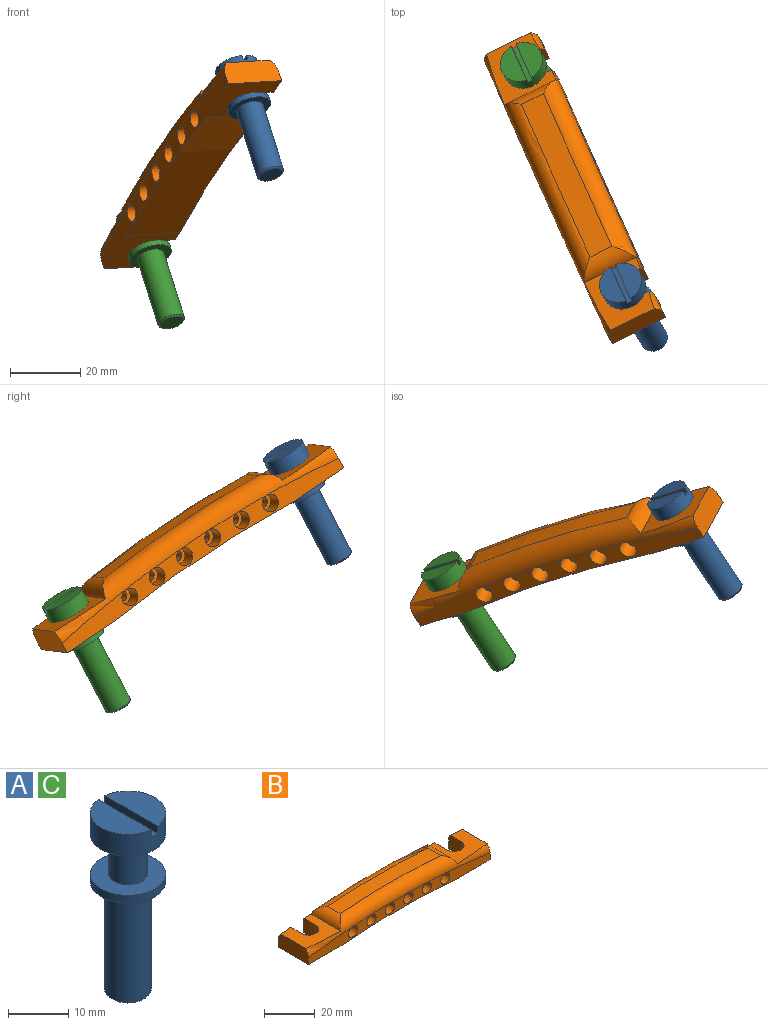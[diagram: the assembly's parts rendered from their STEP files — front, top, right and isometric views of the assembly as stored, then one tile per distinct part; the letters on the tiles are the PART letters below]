
ASSEMBLY  parts=3 mates=1
PART A: 14 faces, bbox 12.5x12.5x36.3 mm
  f0: cylinder r=6.25mm len=12.5mm, axis (0,0,-1), area 168.3mm2, adj f1,f9,f10,f11,f12,f13
  f1: plane 12.41x5.5mm, normal (0,0,1), area 52mm2, adj f0,f13
  f2: plane 6.8x6.8mm, normal (0,0,-1), area 36.3mm2, adj f3
  f3: cone r=3.9mm half-angle=45deg, axis (0,0,1), area 16.2mm2, adj f2,f4
  f4: cylinder r=3.9mm len=21.8mm, axis (0,0,-1), area 534.2mm2, adj f3,f5
  f5: plane 12.5x12.5mm, normal (0,0,-1), area 74.9mm2, adj f4,f6
  f6: cylinder r=6.25mm len=12.5mm, axis (0,0,-1), area 62.8mm2, adj f5,f7
  f7: plane 12.5x12.5mm, normal (0,0,1), area 90.5mm2, adj f6,f8
  f8: cylinder r=3.2mm len=8mm, axis (0,0,-1), area 160.8mm2, adj f7,f9
  f9: plane 12.5x12.5mm, normal (0,0,-1), area 90.5mm2, adj f0,f8
  f10: plane 12.41x5.5mm, normal (0,0,1), area 52mm2, adj f0,f12
  f11: plane 12.5x1.5mm, normal (0,0,1), area 18.7mm2, adj f0,f12,f13
  f12: plane 12.41x1.5mm, normal (-1,0,0), area 18.6mm2, adj f0,f10,f11
  f13: plane 12.41x1.5mm, normal (1,0,0), area 18.6mm2, adj f0,f1,f11
PART B: 42 faces, bbox 103.9x17.1x16 mm
  f0: cylinder r=1.5mm len=12mm, axis (0,1,0), area 113.1mm2, adj f11,f33
  f1: cylinder r=1.5mm len=12mm, axis (0,1,0), area 113.1mm2, adj f11,f41
  f2: cylinder r=1.5mm len=12mm, axis (0,1,0), area 113.1mm2, adj f11,f39
  f3: cylinder r=1.5mm len=12mm, axis (0,1,0), area 113.1mm2, adj f11,f37
  f4: cylinder r=1.5mm len=12mm, axis (0,1,0), area 113.1mm2, adj f11,f35
  f5: cylinder r=1.5mm len=12mm, axis (0,1,0), area 113.1mm2, adj f11,f31
  f6: torus R=351mm, axis (0,-1,0), area 585.5mm2, adj f7,f8,f16,f17,f18,f20,f22,f23
  f7: plane 18.24x16.62mm, normal (0,0,1), area 205.5mm2, adj f6,f13,f14,f16,f23,f27,f28,f29
  f8: plane 18.24x16.62mm, normal (0,0,1), area 205.5mm2, adj f6,f14,f15,f18,f22,f24,f25,f26
  f9: plane 18.15x17mm, normal (0,0,-1), area 227.4mm2, adj f11,f12,f18,f19,f20,f24,f25,f26
  f10: plane 18.15x17mm, normal (0,0,-1), area 227.4mm2, adj f11,f16,f19,f20,f21,f27,f28,f29
  f11: plane 73x6.99mm, normal (0,1,0), area 356.9mm2, adj f0,f1,f2,f3,f4,f5,f9,f10
  f12: plane 6.15x4.15mm, normal (0,1,0), area 23mm2, adj f9,f15,f18,f26
  f13: torus R=351mm, axis (0,-1,0), area 22.1mm2, adj f7,f16,f21,f28
  f14: torus R=351mm, axis (0,-1,0), area 502.2mm2, adj f7,f8,f11,f17,f22,f23,f25,f29
  f15: torus R=351mm, axis (0,-1,0), area 22.1mm2, adj f8,f12,f18,f26
  f16: plane 17.05x7.05mm, normal (1,0,0), area 115.4mm2, adj f6,f7,f10,f13,f20,f21
  f17: cylinder r=356mm len=56.03mm, axis (0,1,0), area 392.6mm2, adj f6,f14,f22,f23
  f18: plane 17.05x7.05mm, normal (-1,0,0), area 115.4mm2, adj f6,f8,f9,f12,f15,f20
  f19: cylinder r=356mm len=65mm, axis (0,1,0), area 1106.5mm2, adj f9,f10,f11,f20
  f20: plane 101.3x6.99mm, normal (0,-1,0), area 397mm2, adj f6,f9,f10,f16,f18,f19,f30,f32
  f21: plane 6.15x4.15mm, normal (0,1,0), area 23mm2, adj f10,f13,f16,f28
  f22: cylinder r=5mm len=16.53mm, axis (0,-1,0), area 79.5mm2, adj f6,f8,f14,f17
  f23: cylinder r=5mm len=16.53mm, axis (0,-1,0), area 79.5mm2, adj f6,f7,f14,f17
  f24: cylinder r=4mm len=8mm, axis (0,0,1), area 88mm2, adj f8,f9,f25,f26
  f25: plane 7.01x7.01mm, normal (-1,0,0), area 48.8mm2, adj f8,f9,f11,f14,f24
  f26: plane 7.02x7.02mm, normal (1,0,0), area 48.2mm2, adj f8,f9,f12,f15,f24
  f27: cylinder r=4mm len=8mm, axis (0,0,1), area 88mm2, adj f7,f10,f28,f29
  f28: plane 7.02x7.02mm, normal (-1,0,0), area 48.2mm2, adj f7,f10,f13,f21,f27
  f29: plane 7.01x7.01mm, normal (1,0,0), area 48.8mm2, adj f7,f10,f11,f14,f27
  f30: cylinder r=2.55mm len=5.1mm, axis (0,-1,0), area 80.1mm2, adj f6,f20,f31
  f31: plane 5.1x5.1mm, normal (0,-1,0), area 13.4mm2, adj f5,f30
  f32: cylinder r=2.55mm len=5.1mm, axis (0,-1,0), area 80.1mm2, adj f6,f20,f33
  f33: plane 5.1x5.1mm, normal (0,-1,0), area 13.4mm2, adj f0,f32
  f34: cylinder r=2.55mm len=5.1mm, axis (0,-1,0), area 80.1mm2, adj f6,f20,f35
  f35: plane 5.1x5.1mm, normal (0,-1,0), area 13.4mm2, adj f4,f34
  f36: cylinder r=2.55mm len=5.1mm, axis (0,-1,0), area 80.1mm2, adj f20,f37
  f37: plane 5.1x5.1mm, normal (0,-1,0), area 13.4mm2, adj f3,f36
  f38: cylinder r=2.55mm len=5.1mm, axis (0,-1,0), area 80.1mm2, adj f20,f39
  f39: plane 5.1x5.1mm, normal (0,-1,0), area 13.4mm2, adj f2,f38
  f40: cylinder r=2.55mm len=5.1mm, axis (0,-1,0), area 80.1mm2, adj f6,f20,f41
  f41: plane 5.1x5.1mm, normal (0,-1,0), area 13.4mm2, adj f1,f40
PART C: same geometry as A
PLACE A rot(axis=(-0.75,-0.25,0.61),40.2deg) t=(673.2,727.66,-308.17)mm
PLACE B rot(axis=(-0.21,-0.42,-0.88),71.3deg) t=(662.55,766.87,-320.16)mm
PLACE C rot(axis=(-0.75,-0.25,0.61),40.2deg) t=(644.89,790.75,-350.37)mm
MATE fastened B.f24 <-> C.f0  axis (-0.27,0.45,0.85) through (641.17,796.91,-338.65)mm
